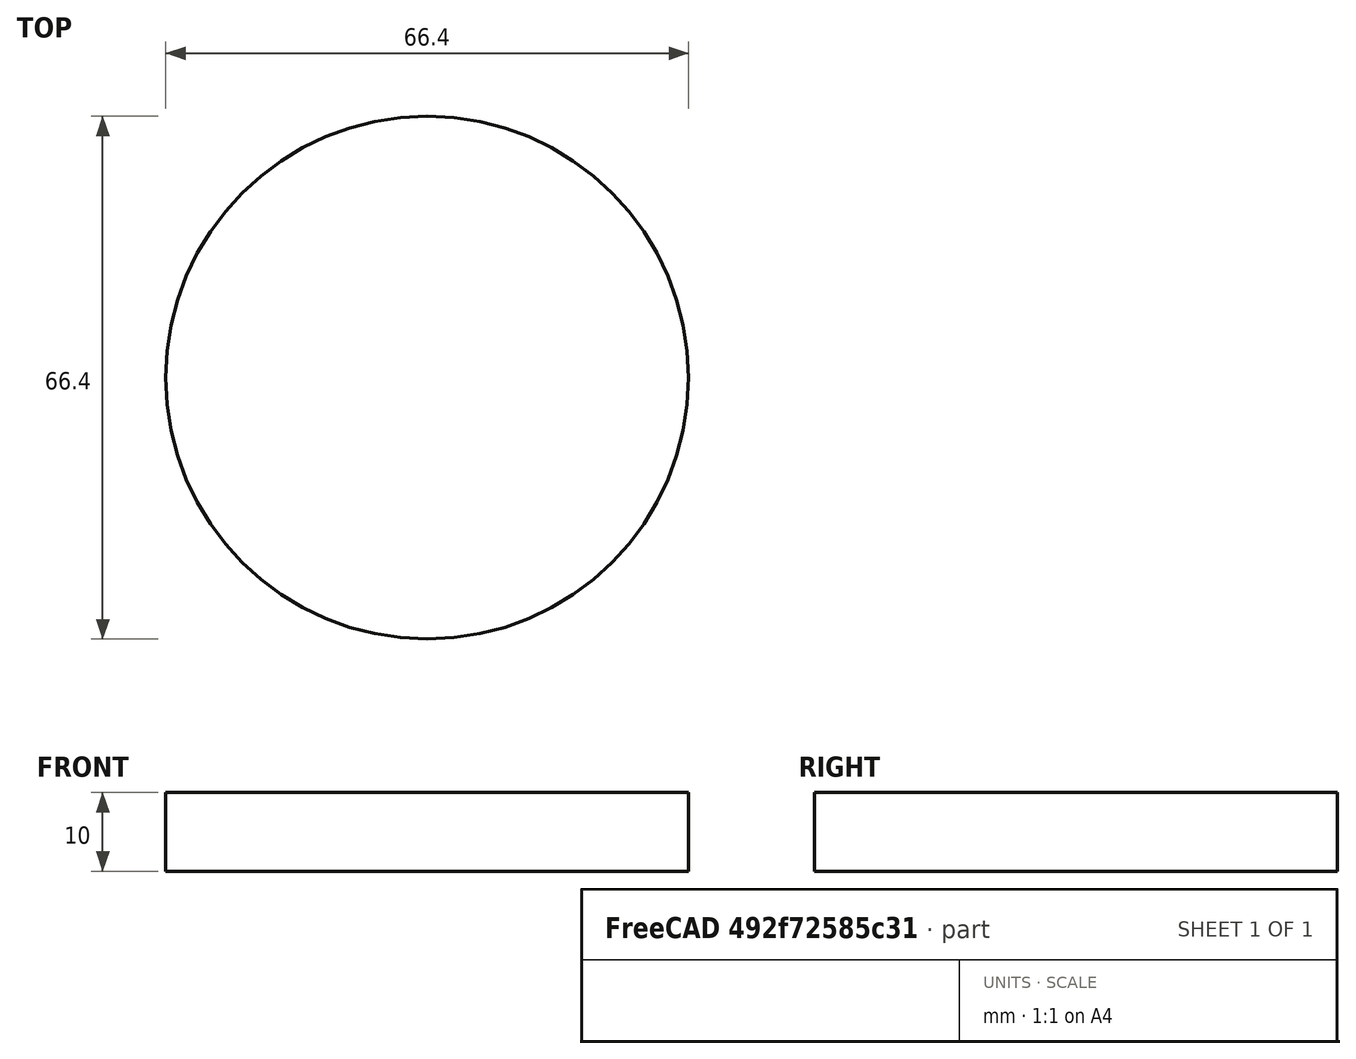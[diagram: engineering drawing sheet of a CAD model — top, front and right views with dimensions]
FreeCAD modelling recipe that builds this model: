
FCSTD DOCUMENT  (FreeCAD 1.0R39109 (Git))
Label: bottom
License: All rights reserved
LicenseURL: https://en.wikipedia.org/wiki/All_rights_reserved
objects: Sketcher::SketchObject×1, PartDesign::Pad×1, PartDesign::Body×1
note: 6 computed .brp shape members not serialized (recipe doc carries the construction recipe); baked Part::Feature solids carry a one-line shape summary decoded from their .brp

FEATURE [Sketcher::SketchObject] Sketch
  ArcFitTolerance = 1e-06
  AttachmentSupport = -> [XY_Plane]
  FullyConstrained = true
  MakeInternals = false
  MapMode = 5
  sketch-geometry (1):
    g0: Circle CenterX=0 CenterY=0 CenterZ=0 NormalX=0 NormalY=0 NormalZ=1 AngleXU=0 Radius=33.2
  constraints (2):
    c: Coincident(g0,g-1)
    c: Diameter(g0) = 66.4
FEATURE [PartDesign::Pad] Pad
  Direction = (0,0,1)
  Length = 10
  Length2 = 10
  Profile = -> Sketch
  ReferenceAxis = -> Sketch [N_Axis]
  Refine = true
  Suppressed = false
  Type = 0
FEATURE [PartDesign::Body] Body
  AllowCompound = false
  Group = -> [Sketch,Pad]
  Origin = -> Origin
  Tip = -> Pad
